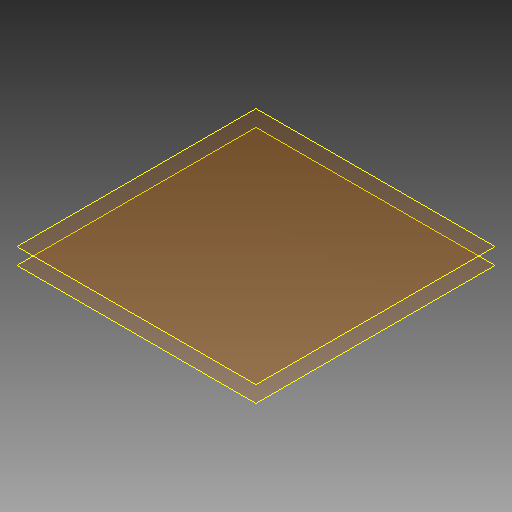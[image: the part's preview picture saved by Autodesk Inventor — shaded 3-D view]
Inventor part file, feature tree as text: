
AUTODESK INVENTOR PART (.ipt)
format: ipt  version: 2019 (Build 230136000, 136)  size: 103,424 bytes
history: native  units: mm
features: plane x2, sketch x2, extrude x1, hole x1
ambient origin geometry x8: Origin, YZ Plane, XZ Plane, XY Plane, X Axis, Y Axis, Z Axis, Center Point
bodies: Solid1 (feature_tree)
feature tree (6):
  plane  "Work Plane1"
  extrude  "Extrusion1"  Depth=51.0mm
  plane  "Work Plane2"
  hole  "Hole1"  [1 undecoded]
  sketch  "Sketch2"  dims[d5=64.0mm d6=51.0mm]
  sketch  "Sketch3"  dims[d7=18.0mm d8=16.0mm d9=1.5mm d10=0.0mm d11=12.0mm d12=10.0mm d13=15.0mm d14=13.0mm d15=16.0mm d16=15.0mm d17=10.0mm d18=3.0mm d19=6.0mm d20=4.0mm d21=2.0mm d22=90.0deg d23=8.0mm d24=20.594885mm d25=18.0mm]
note: 1 required parameter value undecoded (feature->parameter linkage not recoverable at this tier; creation-order binding heuristic only, values carry confidence <= 0.55)
